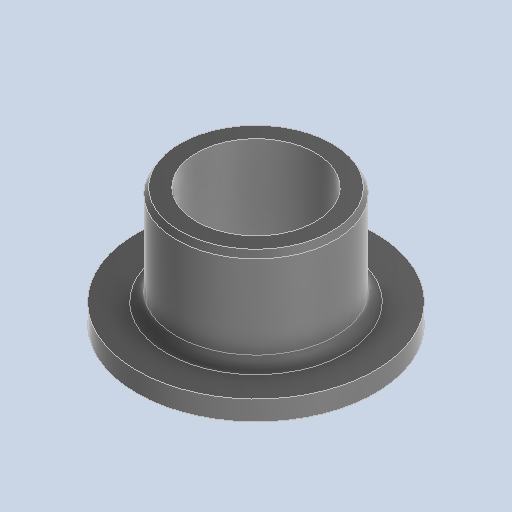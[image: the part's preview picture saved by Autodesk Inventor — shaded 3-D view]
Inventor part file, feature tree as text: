
AUTODESK INVENTOR PART (.ipt)
format: ipt  version: 2024.2 (Build 282272000, 272)  size: 267,264 bytes
history: native  units: mm
features: revolve x1, fillet x1, sketch x1
ambient origin geometry x8: Origin, YZ Plane, XZ Plane, XY Plane, X Axis, Y Axis, Z Axis, Center Point
bodies: Solid1 (feature_tree)
feature tree (3):
  revolve  "Revolution1"  Angle=30.0deg
  fillet  "Fillet1"  Radius=0.5mm
  sketch  "Sketch1"  dims[d5=90.0deg d11=30.0deg d12=0.5mm]
